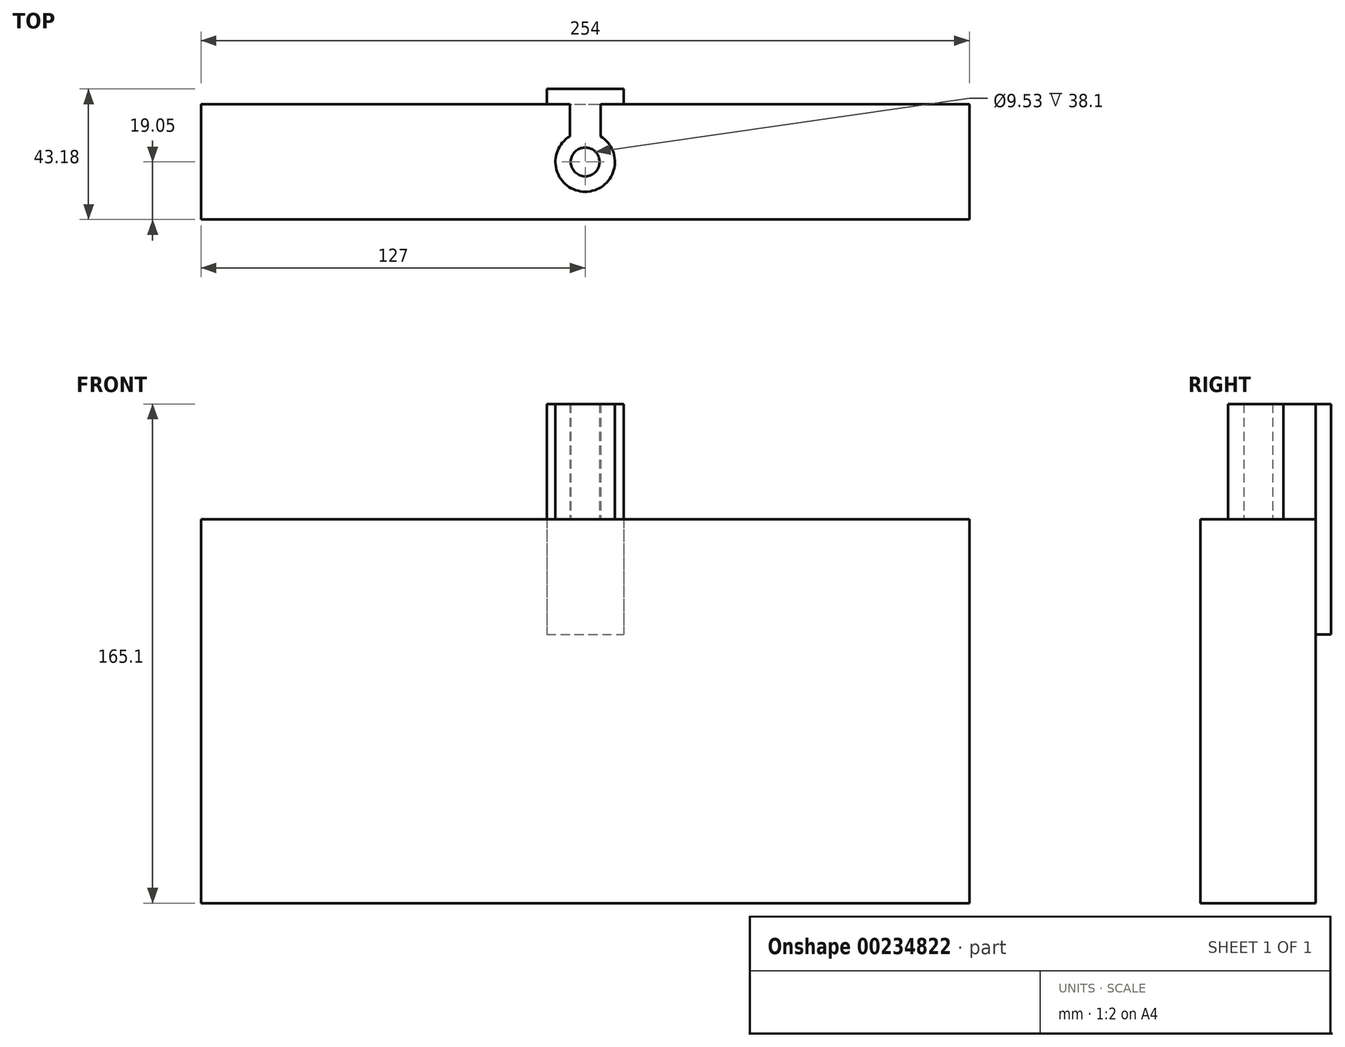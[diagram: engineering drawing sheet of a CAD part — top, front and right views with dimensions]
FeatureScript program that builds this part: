
annotation { "Feature Type Name" : "Feature", "Feature Type Description" : "" }
export const myFeature = defineFeature(function(context is Context, id is Id, definition is map)
    precondition{}
    {
        {
            var Q0;
            Q0=qCreatedBy(makeId("Top.planeOp"),FACE);
            var sketch = newSketch(context, id + "F0", { "sketchPlane" : qUnion([Q0])});
            skLineSegment(sketch, "E0.bottom", {"start": v(-127, 0) * mm, "end": v(127, 0) * mm});
            skLineSegment(sketch, "E0.top", {"start": v(-127, -38.1) * mm, "end": v(127, -38.1) * mm});
            skLineSegment(sketch, "E0.left", {"start": v(-127, 0) * mm, "end": v(-127, -38.1) * mm});
            skLineSegment(sketch, "E0.right", {"start": v(127, 0) * mm, "end": v(127, -38.1) * mm});
            skSolve(sketch);
        }
        {
            var Q0;
            Q0 = qSketchRegion(id + "F0", true);
            extrude(context, id + "F1", {"entities" : qUnion([Q0]), "oppositeDirection" : true, "depth" : 127 * mm});
        }
        {
            var Q0;
            Q0=qCreatedBy(makeId("Top.planeOp"),FACE);
            var sketch = newSketch(context, id + "F2", { "sketchPlane" : qUnion([Q0])});
            skCircle(sketch, "E1", {"center": v(0, -19.05) * mm, "radius": 4.76 * mm});
            skLineSegment(sketch, "E2", {"start": v(0, 0) * mm, "end": v(0, -38.1) * mm});
            skArc(sketch, "E3.0", {"start": v(-5.08, -10.62) * mm, "mid": v(0, -28.9) * mm, "end": v(5.08, -10.62) * mm});
            skLineSegment(sketch, "E4.left", {"start": v(-5.08, -10.62) * mm, "end": v(-5.08, 0) * mm});
            skLineSegment(sketch, "E4.right", {"start": v(5.08, -10.62) * mm, "end": v(5.08, 0) * mm});
            skLineSegment(sketch, "E5.bottom", {"start": v(-12.7, 5.08) * mm, "end": v(12.7, 5.08) * mm});
            skLineSegment(sketch, "E5.top", {"start": v(-12.7, 0) * mm, "end": v(-5.08, 0) * mm});
            skLineSegment(sketch, "E5.left", {"start": v(-12.7, 5.08) * mm, "end": v(-12.7, 0) * mm});
            skLineSegment(sketch, "E5.right", {"start": v(12.7, 5.08) * mm, "end": v(12.7, 0) * mm});
            skLineSegment(sketch, "E6.trimOffspring", {"start": v(5.08, 0) * mm, "end": v(12.7, 0) * mm});
            skLineSegment(sketch, "E7", {"start": v(-5.08, -10.62) * mm, "end": v(5.08, -10.62) * mm, "construction": true});
            skSolve(sketch);
        }
        {
            var Q0;
            Q0 = qSketchRegion(id + "F2", true);
            extrude(context, id + "F3", {"entities" : qUnion([Q0]), "depth" : 38.1 * mm});
        }
        {
            var Q0;
            Q0=makeQuery(id+"F3.opExtrude","CAP_FACE",FACE,{"disambiguationData":[OSD([sQuery(id+"F2.wireOp",EDGE,"E1"),sQuery(id+"F2.wireOp",EDGE,"E3.0"),sQuery(id+"F2.wireOp",EDGE,"E4.left"),sQuery(id+"F2.wireOp",EDGE,"E4.right"),sQuery(id+"F2.wireOp",EDGE,"E5.bottom"),sQuery(id+"F2.wireOp",EDGE,"E5.top"),sQuery(id+"F2.wireOp",EDGE,"E5.left"),sQuery(id+"F2.wireOp",EDGE,"E5.right"),sQuery(id+"F2.wireOp",EDGE,"E6.trimOffspring")])],"isStart":true});
            var sketch = newSketch(context, id + "F4", { "sketchPlane" : qUnion([Q0])});
            skLineSegment(sketch, "E8.bottom", {"start": v(-12.7, -5.08) * mm, "end": v(12.7, -5.08) * mm});
            skLineSegment(sketch, "E8.top", {"start": v(-12.7, 0) * mm, "end": v(12.7, 0) * mm});
            skLineSegment(sketch, "E8.left", {"start": v(-12.7, -5.08) * mm, "end": v(-12.7, 0) * mm});
            skLineSegment(sketch, "E8.right", {"start": v(12.7, -5.08) * mm, "end": v(12.7, 0) * mm});
            skSolve(sketch);
        }
        {
            var Q0;
            Q0 = qSketchRegion(id + "F4", true);
            extrude(context, id + "F5", {"entities" : qUnion([Q0]), "operationType" : NewBodyOperationType.ADD, "depth" : 38.1 * mm});
        }
    });
